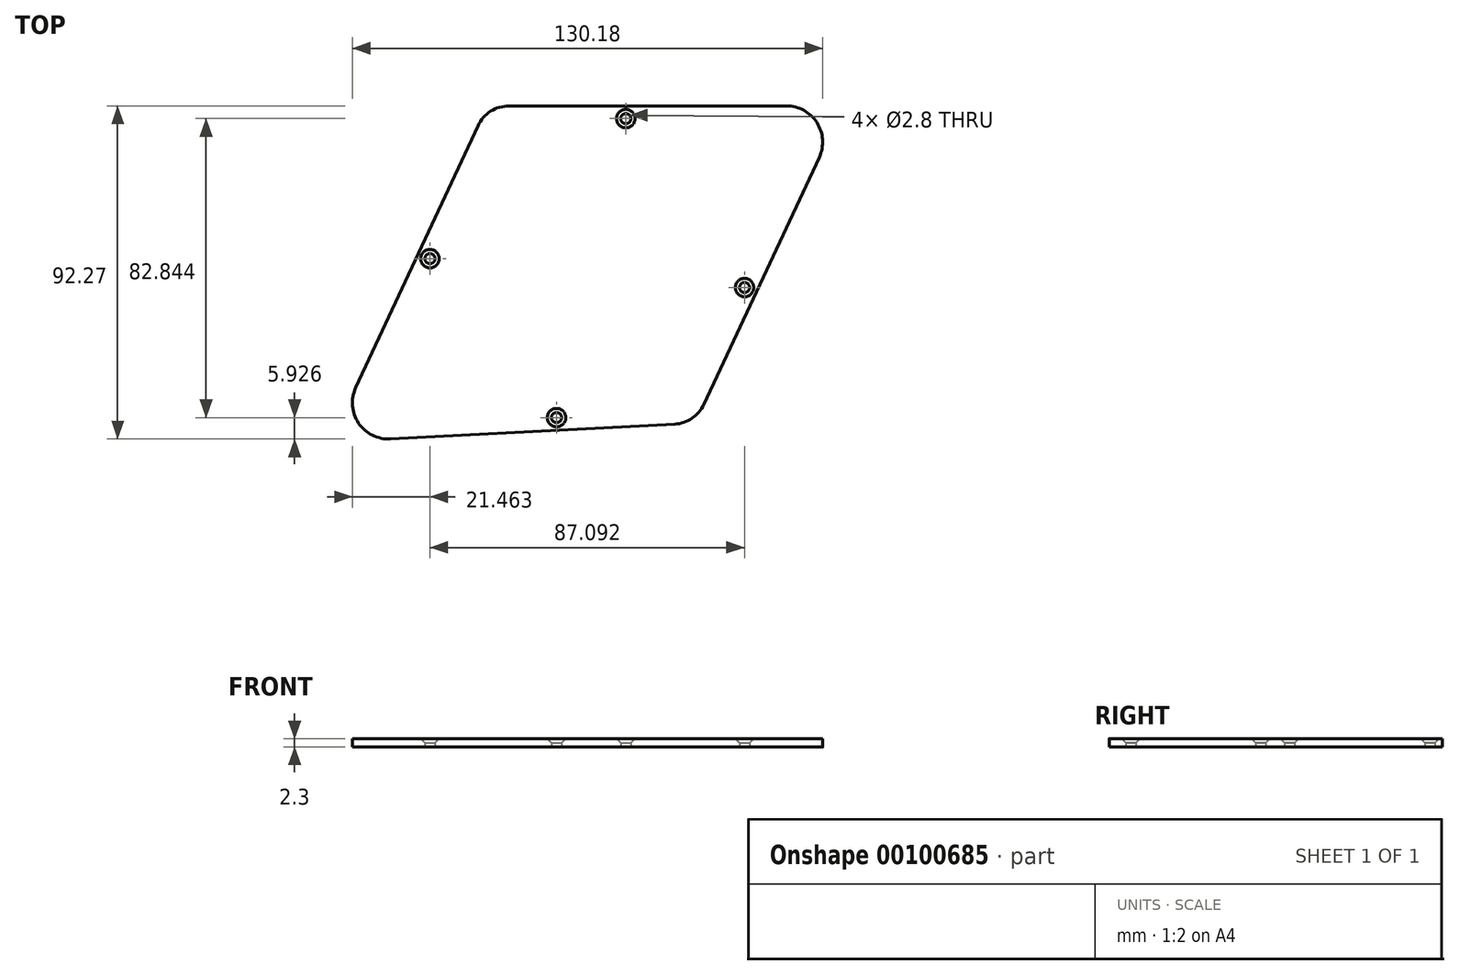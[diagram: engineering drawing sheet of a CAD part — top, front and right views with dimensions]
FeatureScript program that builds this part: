
annotation { "Feature Type Name" : "Feature", "Feature Type Description" : "" }
export const myFeature = defineFeature(function(context is Context, id is Id, definition is map)
    precondition{}
    {
        {
            var Q0;
            Q0=qCreatedBy(makeId("Top.planeOp"),FACE);
            var sketch = newSketch(context, id + "F0", { "sketchPlane" : qUnion([Q0])});
            skLineSegment(sketch, "E0", {"start": v(0, 0) * mm, "end": v(0, 92.8) * mm, "construction": true});
            skLineSegment(sketch, "E1", {"start": v(0, 92.81) * mm, "end": v(130.18, 92.81) * mm, "construction": true});
            skLineSegment(sketch, "E2", {"start": v(130.18, 92.81) * mm, "end": v(130.18, 0) * mm, "construction": true});
            skLineSegment(sketch, "E3", {"start": v(130.18, 0) * mm, "end": v(0, 0) * mm, "construction": true});
            skLineSegment(sketch, "E4", {"start": v(0, 92.81) * mm, "end": v(130.18, 0) * mm, "construction": true});
            skLineSegment(sketch, "E5", {"start": v(0, 0) * mm, "end": v(130.18, 6.82) * mm, "construction": true});
            skPoint(sketch, "E6", {"position": v(55.68, 6.42) * mm});
            skArc(sketch, "E7", {"start": v(0.94, 14.76) * mm, "mid": v(1.7, 4.95) * mm, "end": v(10.52, 0.55) * mm});
            skArc(sketch, "E8", {"start": v(129.24, 78.58) * mm, "mid": v(128.61, 88.18) * mm, "end": v(120.18, 92.81) * mm});
            skLineSegment(sketch, "E9", {"start": v(129.24, 78.58) * mm, "end": v(97.33, 10.15) * mm});
            skArc(sketch, "E10", {"start": v(89.22, 4.68) * mm, "mid": v(94.03, 6.29) * mm, "end": v(97.33, 10.15) * mm});
            skLineSegment(sketch, "E11", {"start": v(89.22, 4.68) * mm, "end": v(10.52, 0.55) * mm});
            skLineSegment(sketch, "E12", {"start": v(0.94, 14.76) * mm, "end": v(34.77, 87.32) * mm});
            skLineSegment(sketch, "E13", {"start": v(43.38, 92.81) * mm, "end": v(120.18, 92.81) * mm});
            skArc(sketch, "E14", {"start": v(43.38, 92.81) * mm, "mid": v(38.28, 91.32) * mm, "end": v(34.77, 87.32) * mm});
            skSolve(sketch);
        }
        {
            var Q0;
            Q0=makeQuery(id+"F0.imprint","IMPRINT",FACE,{"disambiguationData":[TD([[makeQuery(id+"F0.imprint","IMPRINT",EDGE,{"derivedFrom":sQuery(id+"F0.wireOp",EDGE,"E7")}),1.0]])]});
            extrude(context, id + "F1", {"entities" : qUnion([Q0]), "depth" : 2.3 * mm});
        }
        {
            var Q0;
            Q0=makeQuery(id+"F1.opExtrude","CAP_FACE",FACE,{"disambiguationData":[OSD([sQuery(id+"F0.wireOp",EDGE,"E7"),sQuery(id+"F0.wireOp",EDGE,"E8"),sQuery(id+"F0.wireOp",EDGE,"E9"),sQuery(id+"F0.wireOp",EDGE,"E10"),sQuery(id+"F0.wireOp",EDGE,"E11"),sQuery(id+"F0.wireOp",EDGE,"E12"),sQuery(id+"F0.wireOp",EDGE,"E13"),sQuery(id+"F0.wireOp",EDGE,"E14")])],"isStart":false});
            var sketch = newSketch(context, id + "F2", { "sketchPlane" : qUnion([Q0])});
            skPoint(sketch, "E15", {"position": v(21.46, 50.5) * mm});
            skPoint(sketch, "E16", {"position": v(75.68, 89.31) * mm});
            skPoint(sketch, "E17", {"position": v(108.56, 42.5) * mm});
            skPoint(sketch, "E18", {"position": v(56.5, 6.47) * mm});
            skSolve(sketch);
        }
        {
            var Q0;
            Q0=sQuery(id+"F2.wireOp",VERTEX,"E15");
            var Q1;
            Q1=sQuery(id+"F2.wireOp",VERTEX,"E17");
            var Q2;
            Q2=sQuery(id+"F2.wireOp",VERTEX,"E16");
            var Q3;
            Q3=sQuery(id+"F2.wireOp",VERTEX,"E18");
            var Q4;
            Q4=makeQuery(id+"F1.opExtrude","SWEPT_BODY",BODY,{"disambiguationData":[OSD([sQuery(id+"F0.wireOp",EDGE,"E7"),sQuery(id+"F0.wireOp",EDGE,"E8"),sQuery(id+"F0.wireOp",EDGE,"E9"),sQuery(id+"F0.wireOp",EDGE,"E10"),sQuery(id+"F0.wireOp",EDGE,"E11"),sQuery(id+"F0.wireOp",EDGE,"E12"),sQuery(id+"F0.wireOp",EDGE,"E13"),sQuery(id+"F0.wireOp",EDGE,"E14")])]});
            hole(context, id + "F3", {"style" : HoleStyle.C_SINK, "endStyle" : HoleEndStyle.THROUGH, "holeDiameter" : 2.8 * mm, "cSinkDiameter" : 5.1 * mm, "cSinkAngle" : 90 * degree, "locations" : qUnion([Q0, Q1, Q2, Q3]), "scope" : qUnion([Q4]), "isTappedThrough" : true, "startStyle" : HoleStartStyle.PART});
        }
    });
